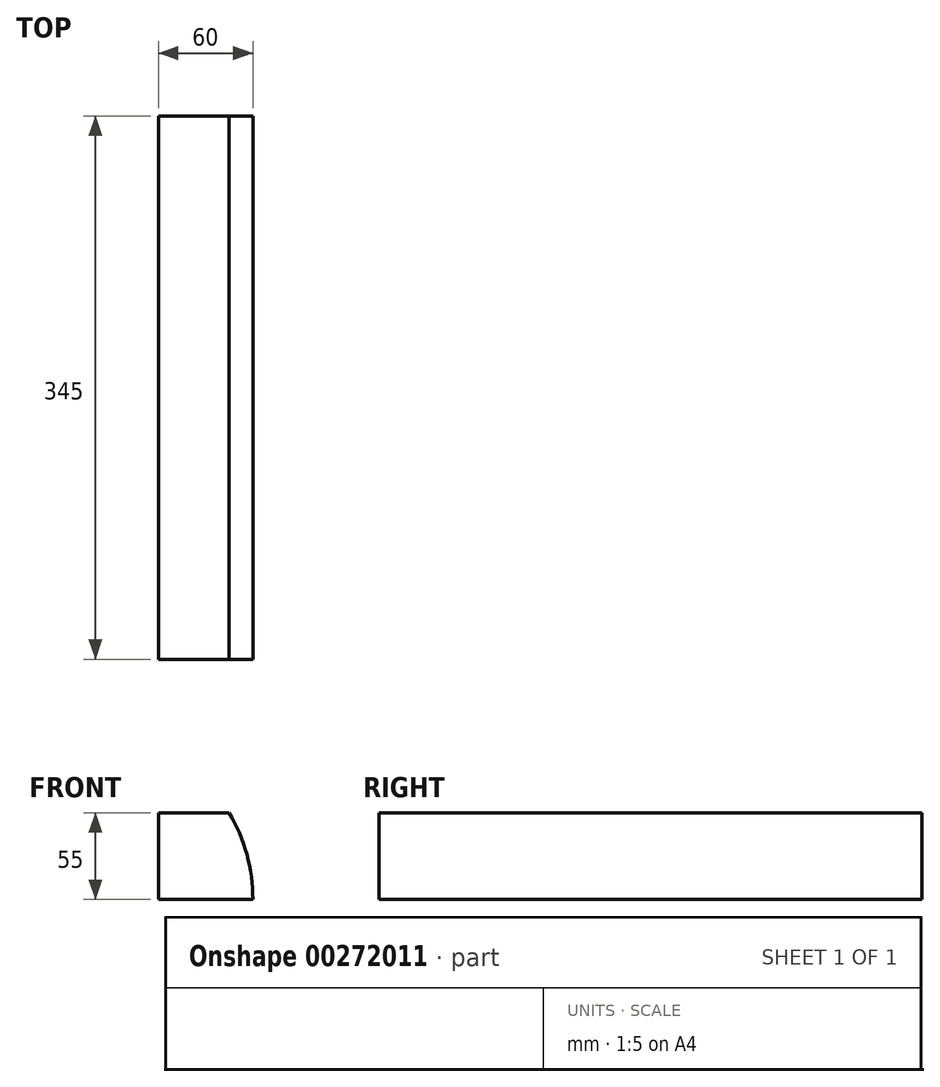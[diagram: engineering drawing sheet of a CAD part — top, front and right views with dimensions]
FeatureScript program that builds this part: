
annotation { "Feature Type Name" : "Feature", "Feature Type Description" : "" }
export const myFeature = defineFeature(function(context is Context, id is Id, definition is map)
    precondition{}
    {
        {
            var Q0;
            Q0=qCreatedBy(makeId("Front.planeOp"),FACE);
            var sketch = newSketch(context, id + "F0", { "sketchPlane" : qUnion([Q0])});
            skLineSegment(sketch, "E0.bottom", {"start": v(0, 0) * mm, "end": v(45, 0) * mm});
            skLineSegment(sketch, "E0.top", {"start": v(0, 110) * mm, "end": v(45, 110) * mm});
            skLineSegment(sketch, "E0.left", {"start": v(0, 0) * mm, "end": v(0, 110) * mm});
            skLineSegment(sketch, "E1", {"start": v(0, 55) * mm, "end": v(60, 55) * mm});
            skArc(sketch, "E2", {"start": v(45, 0) * mm, "mid": v(60, 55) * mm, "end": v(45, 110) * mm});
            skSolve(sketch);
        }
        {
            var Q0;
            {var subQ0=sQuery(id+"F0.wireOp",EDGE,"E0.top");Q0=makeQuery(id+"F0.imprint","IMPRINT",FACE,{"disambiguationData":[TD([[makeQuery(id+"F0.imprint","IMPRINT",EDGE,{"derivedFrom":subQ0}),-1.0]])]});}
            extrude(context, id + "F1", {"entities" : qUnion([Q0]), "oppositeDirection" : true, "depth" : 345 * mm});
        }
    });
